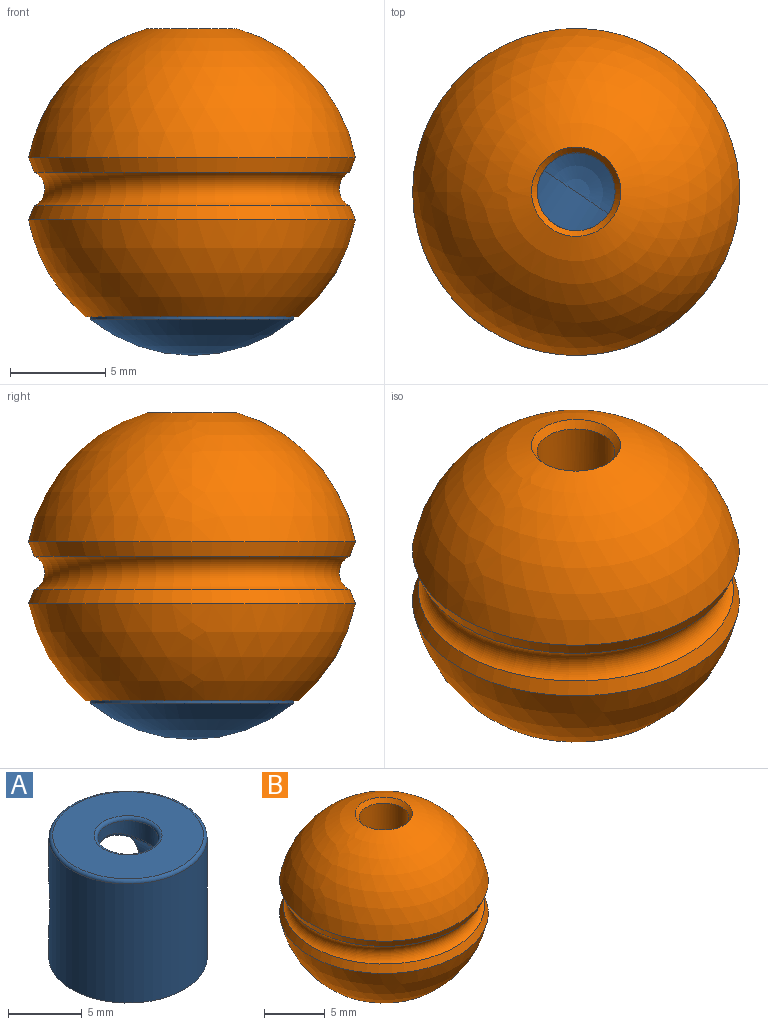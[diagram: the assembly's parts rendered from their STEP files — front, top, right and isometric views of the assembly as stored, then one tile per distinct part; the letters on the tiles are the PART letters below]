
ASSEMBLY  parts=2 mates=1
PART A: 11 faces, bbox 11.6x11.6x12 mm
  f0: sphere r=8.5mm, area 101.2mm2, adj f3
  f1: sphere r=4.15mm, area 100.2mm2, adj f4,f7
  f2: cylinder r=2.05mm len=4.1mm, axis (0,0,-1), area 17.3mm2, adj f7,f8,f9
  f3: cylinder r=5.35mm len=10.7mm, axis (0,0,-1), area 265.6mm2, adj f0,f5,f10
  f4: cylinder r=4.15mm len=8.3mm, axis (0,-1,0), area 101.1mm2, adj f1,f5,f8
  f5: bspline ~8.76x8.56mm, area 7.1mm2, adj f3,f4
  f6: plane 10.2x10.2mm, normal (0,0,1), area 65.1mm2, adj f9,f10
  f7: torus R=2.3mm, axis (0,0,-1), area 1.7mm2, adj f1,f2,f8
  f8: bspline ~4.34x2.76mm, area 2.2mm2, adj f2,f4,f7
  f9: torus R=2.3mm, axis (0,0,-1), area 5.3mm2, adj f2,f6
  f10: torus R=5.1mm, axis (0,0,-1), area 13mm2, adj f3,f6
PART B: 11 faces, bbox 18.9x18.9x15.2 mm
  f0: cylinder r=2.05mm len=4.4mm, axis (0,0,-1), area 56.7mm2, adj f1,f9
  f1: cone r=2.35mm half-angle=36.9deg, axis (0,0,1), area 6.9mm2, adj f0,f2
  f2: sphere r=8.75mm, area 373.8mm2, adj f1,f3
  f3: cone r=8.29mm half-angle=22.3deg, axis (0,0,1), area 42.4mm2, adj f2,f4
  f4: torus R=8.75mm, axis (0,0,-1), area 109.3mm2, adj f3,f5
  f5: cone r=8.29mm half-angle=22.3deg, axis (0,0,-1), area 42.4mm2, adj f4,f6
  f6: sphere r=8.75mm, area 280.5mm2, adj f5,f7
  f7: cylinder r=5.59mm len=11.18mm, axis (0,0,-1), area 337.4mm2, adj f6,f10
  f8: plane 10.43x10.43mm, normal (0,0,-1), area 67mm2, adj f9,f10
  f9: torus R=2.43mm, axis (0,0,1), area 8.1mm2, adj f0,f8
  f10: torus R=5.22mm, axis (0,0,1), area 20.2mm2, adj f7,f8
PLACE A rot(axis=(0,0,1),146.1deg) t=(0,0,-3.5)mm
PLACE B t=(0,0,-3.25)mm
MATE cylindrical A.f2 <-> B.f0  axis (0,0,1) through (0,0,0)mm
